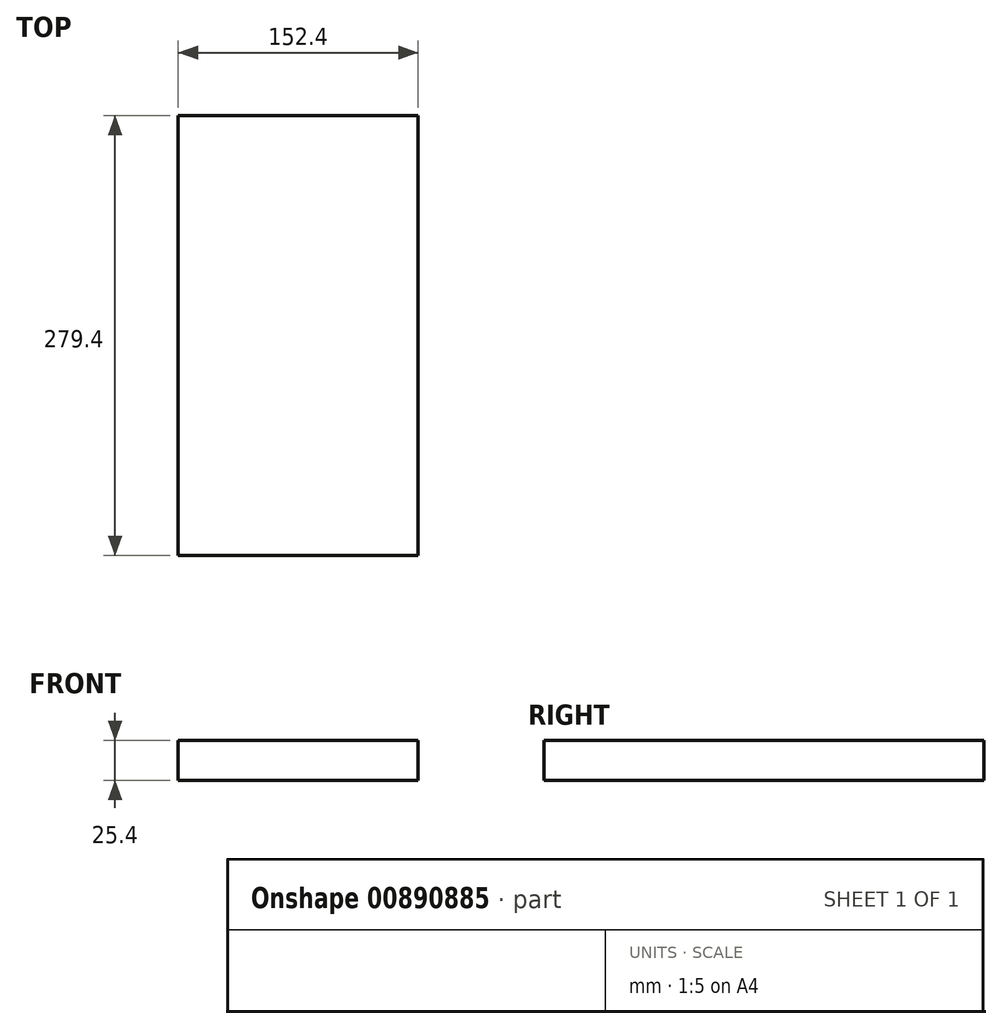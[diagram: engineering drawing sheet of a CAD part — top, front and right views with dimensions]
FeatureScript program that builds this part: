
annotation { "Feature Type Name" : "Feature", "Feature Type Description" : "" }
export const myFeature = defineFeature(function(context is Context, id is Id, definition is map)
    precondition{}
    {
        {
            var Q0;
            Q0=qCreatedBy(makeId("Top.planeOp"),FACE);
            var sketch = newSketch(context, id + "F0", { "sketchPlane" : qUnion([Q0])});
            skLineSegment(sketch, "E0.bottom", {"start": v(0, 0) * mm, "end": v(-152.4, 0) * mm});
            skLineSegment(sketch, "E0.top", {"start": v(0, 279.4) * mm, "end": v(-152.4, 279.4) * mm});
            skLineSegment(sketch, "E0.left", {"start": v(0, 0) * mm, "end": v(0, 279.4) * mm});
            skLineSegment(sketch, "E0.right", {"start": v(-152.4, 0) * mm, "end": v(-152.4, 279.4) * mm});
            skSolve(sketch);
        }
        {
            var Q0;
            Q0=makeQuery(id+"F0.imprint","IMPRINT",FACE,{"disambiguationData":[TD([[makeQuery(id+"F0.imprint","IMPRINT",EDGE,{"derivedFrom":sQuery(id+"F0.wireOp",EDGE,"E0.bottom")}),-1.0]])]});
            extrude(context, id + "F1", {"entities" : qUnion([Q0]), "depth" : 25.4 * mm, "offsetDistance" : 25.4 * mm});
        }
    });
